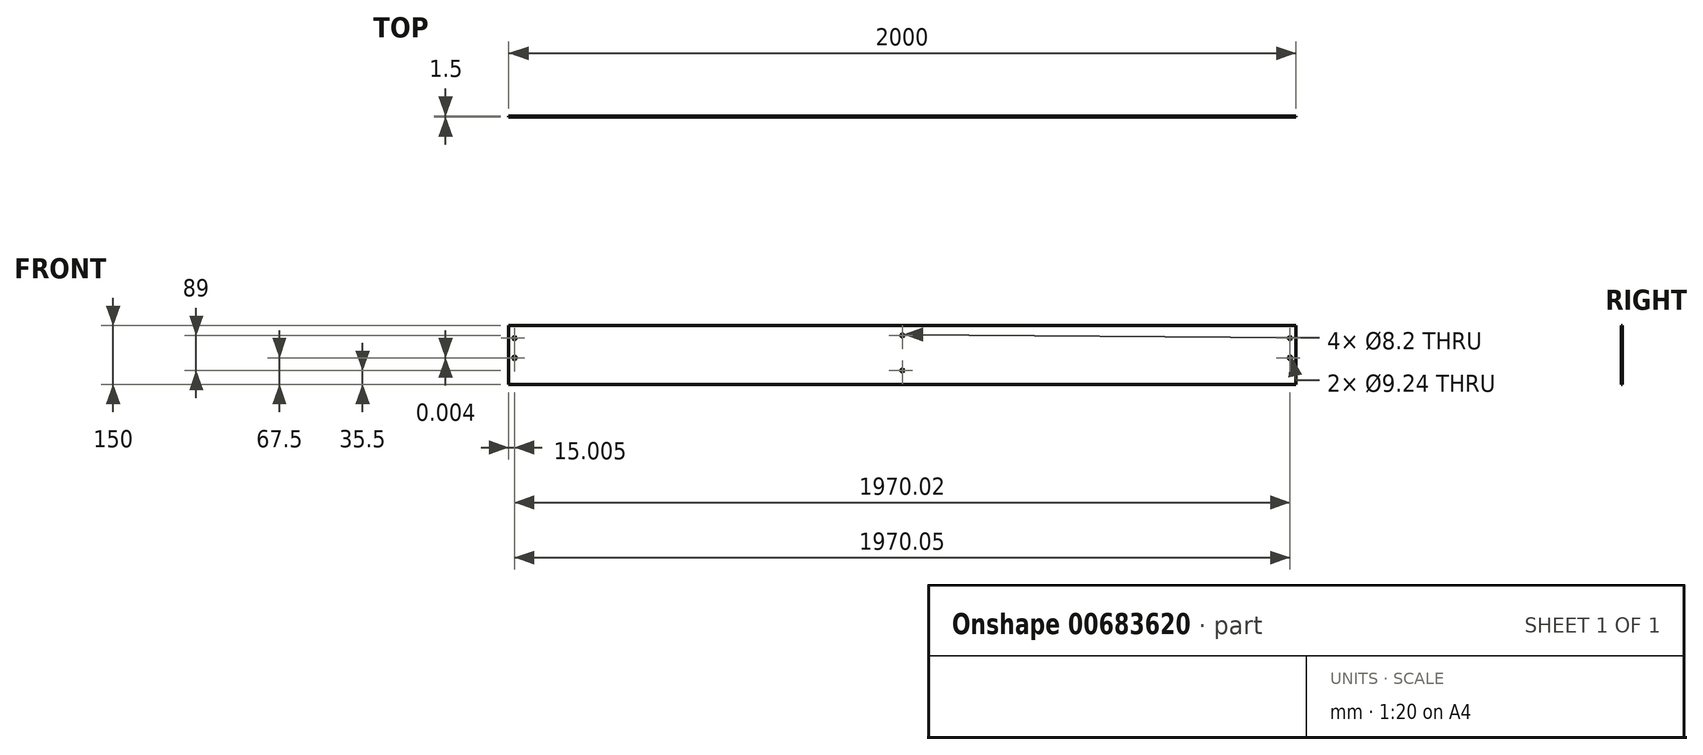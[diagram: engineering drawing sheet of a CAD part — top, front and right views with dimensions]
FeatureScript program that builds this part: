
annotation { "Feature Type Name" : "Feature", "Feature Type Description" : "" }
export const myFeature = defineFeature(function(context is Context, id is Id, definition is map)
    precondition{}
    {
        {
            var Q0;
            Q0=qCreatedBy(makeId("Front.planeOp"),FACE);
            var sketch = newSketch(context, id + "F0", { "sketchPlane" : qUnion([Q0])});
            skCircle(sketch, "E0", {"center": v(856.2, 431.7) * mm, "radius": 4.62 * mm});
            skLineSegment(sketch, "E1", {"start": v(-1128.85, 514.2) * mm, "end": v(871.15, 514.2) * mm});
            skLineSegment(sketch, "E2", {"start": v(-1128.85, 514.2) * mm, "end": v(-1128.85, 364.2) * mm});
            skLineSegment(sketch, "E3", {"start": v(871.15, 514.2) * mm, "end": v(871.15, 364.2) * mm});
            skCircle(sketch, "E4", {"center": v(856.18, 481.7) * mm, "radius": 4.1 * mm});
            skLineSegment(sketch, "E5", {"start": v(-1128.85, 489.04) * mm, "end": v(-1128.85, 514.2) * mm});
            skCircle(sketch, "E6", {"center": v(-1113.85, 481.7) * mm, "radius": 4.1 * mm});
            skCircle(sketch, "E7", {"center": v(-1113.85, 431.7) * mm, "radius": 4.62 * mm});
            skCircle(sketch, "E8", {"center": v(-128.85, 488.7) * mm, "radius": 4.1 * mm});
            skCircle(sketch, "E9", {"center": v(-128.85, 399.7) * mm, "radius": 4.1 * mm});
            skLineSegment(sketch, "E10.0", {"start": v(-1128.85, 364.2) * mm, "end": v(871.15, 364.2) * mm});
            skSolve(sketch);
        }
        {
            var Q0;
            Q0 = qSketchRegion(id + "F0", true);
            extrude(context, id + "F1", {"entities" : qUnion([Q0]), "depth" : 1.5 * mm, "offsetDistance" : 25 * mm});
        }
    });
